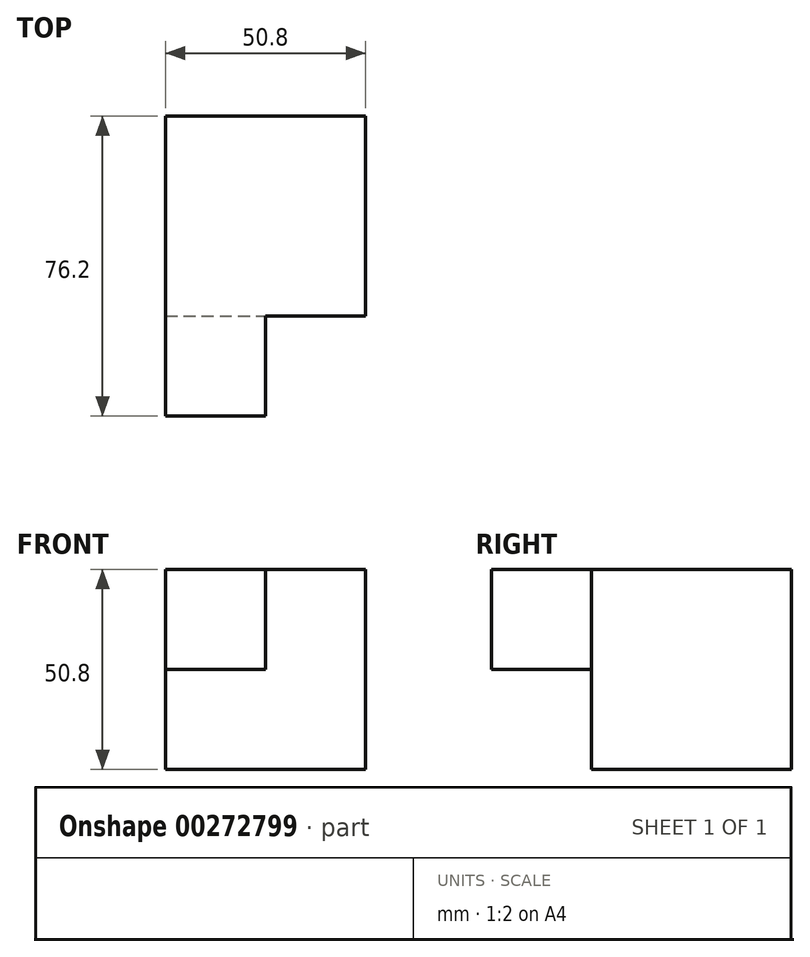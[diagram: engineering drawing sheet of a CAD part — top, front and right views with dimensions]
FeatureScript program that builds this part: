
annotation { "Feature Type Name" : "Feature", "Feature Type Description" : "" }
export const myFeature = defineFeature(function(context is Context, id is Id, definition is map)
    precondition{}
    {
        {
            var Q0;
            Q0=qCreatedBy(makeId("Front.planeOp"),FACE);
            var sketch = newSketch(context, id + "F0", { "sketchPlane" : qUnion([Q0])});
            skLineSegment(sketch, "E0", {"start": v(0, 0) * mm, "end": v(-50.8, 0) * mm});
            skLineSegment(sketch, "E1", {"start": v(-50.8, 0) * mm, "end": v(-50.8, 50.8) * mm});
            skLineSegment(sketch, "E2", {"start": v(-50.8, 50.8) * mm, "end": v(0, 50.8) * mm});
            skLineSegment(sketch, "E3", {"start": v(0, 50.8) * mm, "end": v(0, 0) * mm});
            skSolve(sketch);
        }
        {
            var Q0;
            Q0 = qSketchRegion(id + "F0", true);
            extrude(context, id + "F1", {"entities" : qUnion([Q0]), "depth" : 50.8 * mm});
        }
        {
            var Q0;
            Q0=makeQuery(id+"F1.opExtrude","CAP_FACE",FACE,{"disambiguationData":[OSD([sQuery(id+"F0.wireOp",EDGE,"E0"),sQuery(id+"F0.wireOp",EDGE,"E1"),sQuery(id+"F0.wireOp",EDGE,"E2"),sQuery(id+"F0.wireOp",EDGE,"E3")])],"isStart":false});
            var sketch = newSketch(context, id + "F2", { "sketchPlane" : qUnion([Q0])});
            skLineSegment(sketch, "E4.bottom", {"start": v(-50.8, 50.8) * mm, "end": v(-25.4, 50.8) * mm});
            skLineSegment(sketch, "E4.top", {"start": v(-50.8, 25.4) * mm, "end": v(-25.4, 25.4) * mm});
            skLineSegment(sketch, "E4.left", {"start": v(-50.8, 50.8) * mm, "end": v(-50.8, 25.4) * mm});
            skLineSegment(sketch, "E4.right", {"start": v(-25.4, 50.8) * mm, "end": v(-25.4, 25.4) * mm});
            skSolve(sketch);
        }
        {
            var Q0;
            Q0 = qSketchRegion(id + "F2", true);
            extrude(context, id + "F3", {"entities" : qUnion([Q0]), "operationType" : NewBodyOperationType.ADD, "depth" : 25.4 * mm});
        }
    });
